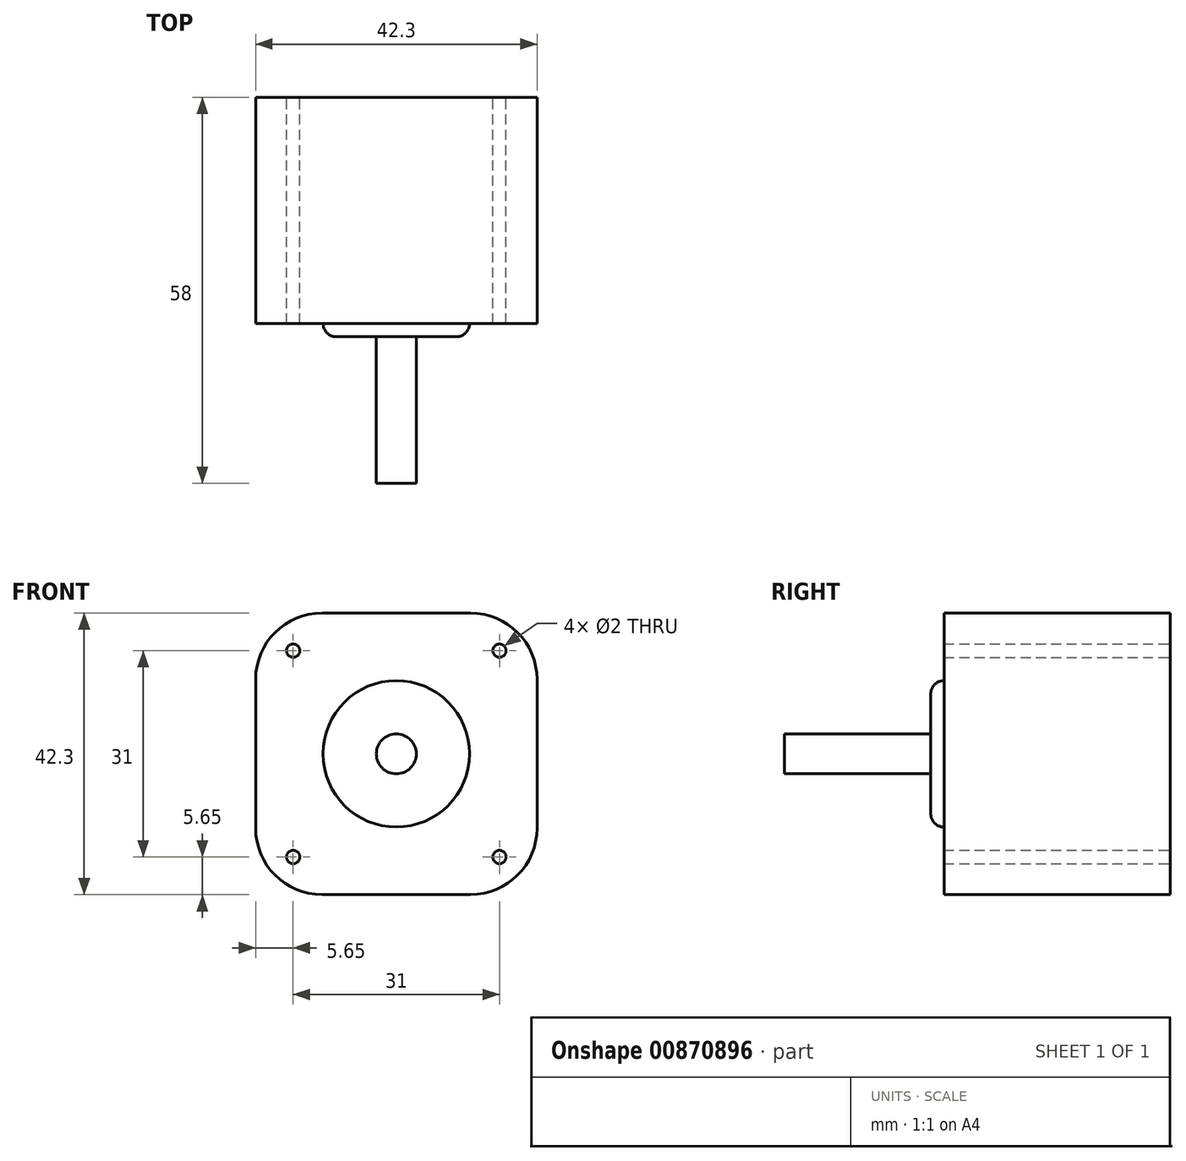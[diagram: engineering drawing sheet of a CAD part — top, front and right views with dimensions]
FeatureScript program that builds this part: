
annotation { "Feature Type Name" : "Feature", "Feature Type Description" : "" }
export const myFeature = defineFeature(function(context is Context, id is Id, definition is map)
    precondition{}
    {
        {
            var Q0;
            Q0=qCreatedBy(makeId("Front.planeOp"),FACE);
            var sketch = newSketch(context, id + "F0", { "sketchPlane" : qUnion([Q0])});
            skPoint(sketch, "E0", {"position": v(0, 21.15) * mm});
            skLineSegment(sketch, "E1", {"start": v(-21.15, 21.15) * mm, "end": v(21.15, 21.15) * mm});
            skLineSegment(sketch, "E2", {"start": v(-21.15, 21.15) * mm, "end": v(-21.15, -21.15) * mm});
            skLineSegment(sketch, "E3", {"start": v(-21.15, -21.15) * mm, "end": v(21.15, -21.15) * mm});
            skLineSegment(sketch, "E4", {"start": v(21.15, -21.15) * mm, "end": v(21.15, 21.15) * mm});
            skSolve(sketch);
        }
        {
            var Q0;
            Q0=makeQuery(id+"F0.imprint","IMPRINT",FACE,{"disambiguationData":[TD([[makeQuery(id+"F0.imprint","IMPRINT",EDGE,{"derivedFrom":sQuery(id+"F0.wireOp",EDGE,"E1")}),-1.0]])]});
            extrude(context, id + "F1", {"entities" : qUnion([Q0]), "depth" : 34 * mm, "offsetDistance" : 25 * mm});
        }
        {
            var Q0;
            Q0=makeQuery(id+"F1.opExtrude","CAP_FACE",FACE,{"disambiguationData":[OSD([sQuery(id+"F0.wireOp",EDGE,"E1"),sQuery(id+"F0.wireOp",EDGE,"E2"),sQuery(id+"F0.wireOp",EDGE,"E3"),sQuery(id+"F0.wireOp",EDGE,"E4")])],"isStart":false});
            var sketch = newSketch(context, id + "F2", { "sketchPlane" : qUnion([Q0])});
            skCircle(sketch, "E5", {"center": v(0, 0) * mm, "radius": 3 * mm});
            skSolve(sketch);
        }
        {
            var Q0;
            Q0 = qSketchRegion(id + "F2", true);
            extrude(context, id + "F3", {"entities" : qUnion([Q0]), "operationType" : NewBodyOperationType.ADD, "depth" : 24 * mm, "offsetDistance" : 25 * mm});
        }
        {
            var Q0;
            Q0=makeQuery(id+"F1.opExtrude","CAP_FACE",FACE,{"disambiguationData":[OSD([sQuery(id+"F0.wireOp",EDGE,"E1"),sQuery(id+"F0.wireOp",EDGE,"E2"),sQuery(id+"F0.wireOp",EDGE,"E3"),sQuery(id+"F0.wireOp",EDGE,"E4")])],"isStart":true});
            var sketch = newSketch(context, id + "F4", { "sketchPlane" : qUnion([Q0])});
            skPoint(sketch, "E6", {"position": v(0, 15.5) * mm});
            skLineSegment(sketch, "E7", {"start": v(-15.5, 15.5) * mm, "end": v(15.5, 15.5) * mm});
            skLineSegment(sketch, "E8", {"start": v(-15.5, 15.5) * mm, "end": v(-15.5, -15.5) * mm});
            skLineSegment(sketch, "E9", {"start": v(-15.5, -15.5) * mm, "end": v(15.5, -15.5) * mm});
            skLineSegment(sketch, "E10", {"start": v(15.5, -15.5) * mm, "end": v(15.5, 15.5) * mm});
            skCircle(sketch, "E11", {"center": v(-15.5, 15.5) * mm, "radius": 1 * mm});
            skCircle(sketch, "E12", {"center": v(-15.5, -15.5) * mm, "radius": 1 * mm});
            skCircle(sketch, "E13", {"center": v(15.5, -15.5) * mm, "radius": 1 * mm});
            skCircle(sketch, "E14", {"center": v(15.5, 15.5) * mm, "radius": 1 * mm});
            skSolve(sketch);
        }
        {
            var Q0;
            {var subQ0=sQuery(id+"F4.wireOp",EDGE,"E8");var subQ1=sQuery(id+"F4.wireOp",EDGE,"E7");var subQ2=makeQuery(id+"F4.imprint","INTERSECT",VERTEX,{"derivedFrom":[subQ1,subQ0]});Q0=makeQuery(id+"F4.imprint","IMPRINT",FACE,{"disambiguationData":[TD([[makeQuery(id+"F4.imprint","IMPRINT",EDGE,{"disambiguationData":[TD([[subQ2,-1.0]])],"derivedFrom":subQ1}),1.0]])]});}
            var Q1;
            {var subQ0=sQuery(id+"F4.wireOp",EDGE,"E10");var subQ1=sQuery(id+"F4.wireOp",EDGE,"E7");var subQ2=makeQuery(id+"F4.imprint","INTERSECT",VERTEX,{"derivedFrom":[subQ1,subQ0]});Q1=makeQuery(id+"F4.imprint","IMPRINT",FACE,{"disambiguationData":[TD([[makeQuery(id+"F4.imprint","IMPRINT",EDGE,{"disambiguationData":[TD([[subQ2,1.0]])],"derivedFrom":subQ1}),1.0]])]});}
            var Q2;
            {var subQ0=sQuery(id+"F4.wireOp",EDGE,"E9");var subQ1=sQuery(id+"F4.wireOp",EDGE,"E8");var subQ2=makeQuery(id+"F4.imprint","INTERSECT",VERTEX,{"derivedFrom":[subQ1,subQ0]});Q2=makeQuery(id+"F4.imprint","IMPRINT",FACE,{"disambiguationData":[TD([[makeQuery(id+"F4.imprint","IMPRINT",EDGE,{"disambiguationData":[TD([[subQ2,1.0]])],"derivedFrom":subQ1}),-1.0]])]});}
            var Q3;
            {var subQ0=sQuery(id+"F4.wireOp",EDGE,"E10");var subQ1=sQuery(id+"F4.wireOp",EDGE,"E9");var subQ2=makeQuery(id+"F4.imprint","INTERSECT",VERTEX,{"derivedFrom":[subQ1,subQ0]});Q3=makeQuery(id+"F4.imprint","IMPRINT",FACE,{"disambiguationData":[TD([[makeQuery(id+"F4.imprint","IMPRINT",EDGE,{"disambiguationData":[TD([[subQ2,1.0]])],"derivedFrom":subQ1}),-1.0]])]});}
            var Q4;
            {var subQ0=sQuery(id+"F4.wireOp",EDGE,"E10");var subQ1=sQuery(id+"F4.wireOp",EDGE,"E7");var subQ2=makeQuery(id+"F4.imprint","INTERSECT",VERTEX,{"derivedFrom":[subQ1,subQ0]});Q4=makeQuery(id+"F4.imprint","IMPRINT",FACE,{"disambiguationData":[TD([[makeQuery(id+"F4.imprint","IMPRINT",EDGE,{"disambiguationData":[TD([[subQ2,1.0]])],"derivedFrom":subQ1}),-1.0]])]});}
            var Q5;
            {var subQ0=sQuery(id+"F4.wireOp",EDGE,"E8");var subQ1=sQuery(id+"F4.wireOp",EDGE,"E7");var subQ2=makeQuery(id+"F4.imprint","INTERSECT",VERTEX,{"derivedFrom":[subQ1,subQ0]});Q5=makeQuery(id+"F4.imprint","IMPRINT",FACE,{"disambiguationData":[TD([[makeQuery(id+"F4.imprint","IMPRINT",EDGE,{"disambiguationData":[TD([[subQ2,-1.0]])],"derivedFrom":subQ1}),-1.0]])]});}
            var Q6;
            {var subQ0=sQuery(id+"F4.wireOp",EDGE,"E9");var subQ1=sQuery(id+"F4.wireOp",EDGE,"E8");var subQ2=makeQuery(id+"F4.imprint","INTERSECT",VERTEX,{"derivedFrom":[subQ1,subQ0]});Q6=makeQuery(id+"F4.imprint","IMPRINT",FACE,{"disambiguationData":[TD([[makeQuery(id+"F4.imprint","IMPRINT",EDGE,{"disambiguationData":[TD([[subQ2,1.0]])],"derivedFrom":subQ1}),1.0]])]});}
            var Q7;
            {var subQ0=sQuery(id+"F4.wireOp",EDGE,"E10");var subQ1=sQuery(id+"F4.wireOp",EDGE,"E9");var subQ2=makeQuery(id+"F4.imprint","INTERSECT",VERTEX,{"derivedFrom":[subQ1,subQ0]});Q7=makeQuery(id+"F4.imprint","IMPRINT",FACE,{"disambiguationData":[TD([[makeQuery(id+"F4.imprint","IMPRINT",EDGE,{"disambiguationData":[TD([[subQ2,1.0]])],"derivedFrom":subQ1}),1.0]])]});}
            extrude(context, id + "F5", {"entities" : qUnion([Q0, Q1, Q2, Q3, Q4, Q5, Q6, Q7]), "operationType" : NewBodyOperationType.REMOVE, "endBound" : BoundingType.THROUGH_ALL, "oppositeDirection" : true, "depth" : 25 * mm, "offsetDistance" : 25 * mm});
        }
        {
            var Q0;
            Q0=makeQuery(id+"F1.opExtrude","CAP_FACE",FACE,{"disambiguationData":[OSD([sQuery(id+"F0.wireOp",EDGE,"E1"),sQuery(id+"F0.wireOp",EDGE,"E2"),sQuery(id+"F0.wireOp",EDGE,"E3"),sQuery(id+"F0.wireOp",EDGE,"E4")])],"isStart":false});
            var sketch = newSketch(context, id + "F6", { "sketchPlane" : qUnion([Q0])});
            skCircle(sketch, "E15", {"center": v(0, 0) * mm, "radius": 11 * mm});
            skSolve(sketch);
        }
        {
            var Q0;
            Q0 = qSketchRegion(id + "F6", true);
            extrude(context, id + "F7", {"entities" : qUnion([Q0]), "operationType" : NewBodyOperationType.ADD, "depth" : 2 * mm, "offsetDistance" : 25 * mm});
        }
        {
            var Q0;
            Q0=makeQuery(id+"F1.opExtrude","SWEPT_EDGE",EDGE,{"disambiguationData":[OSD([sQuery(id+"F0.wireOp",EDGE,"E1"),sQuery(id+"F0.wireOp",EDGE,"E4")])]});
            var Q1;
            Q1=makeQuery(id+"F1.opExtrude","SWEPT_EDGE",EDGE,{"disambiguationData":[OSD([sQuery(id+"F0.wireOp",EDGE,"E1"),sQuery(id+"F0.wireOp",EDGE,"E2")])]});
            var Q2;
            Q2=makeQuery(id+"F1.opExtrude","SWEPT_EDGE",EDGE,{"disambiguationData":[OSD([sQuery(id+"F0.wireOp",EDGE,"E3"),sQuery(id+"F0.wireOp",EDGE,"E4")])]});
            var Q3;
            Q3=makeQuery(id+"F1.opExtrude","SWEPT_EDGE",EDGE,{"disambiguationData":[OSD([sQuery(id+"F0.wireOp",EDGE,"E2"),sQuery(id+"F0.wireOp",EDGE,"E3")])]});
            fillet(context, id + "F8", {"entities" : qUnion([Q0, Q1, Q2, Q3]), "radius" : 10 * mm, "tangentPropagation" : true, "allowEdgeOverflow" : false});
        }
        {
            var Q0;
            Q0=makeQuery(id+"F7.opExtrude","CAP_EDGE",EDGE,{"disambiguationData":[OSD([sQuery(id+"F6.wireOp",EDGE,"E15")])],"isStart":false});
            fillet(context, id + "F9", {"entities" : qUnion([Q0]), "radius" : 2 * mm, "tangentPropagation" : true, "allowEdgeOverflow" : false});
        }
    });
